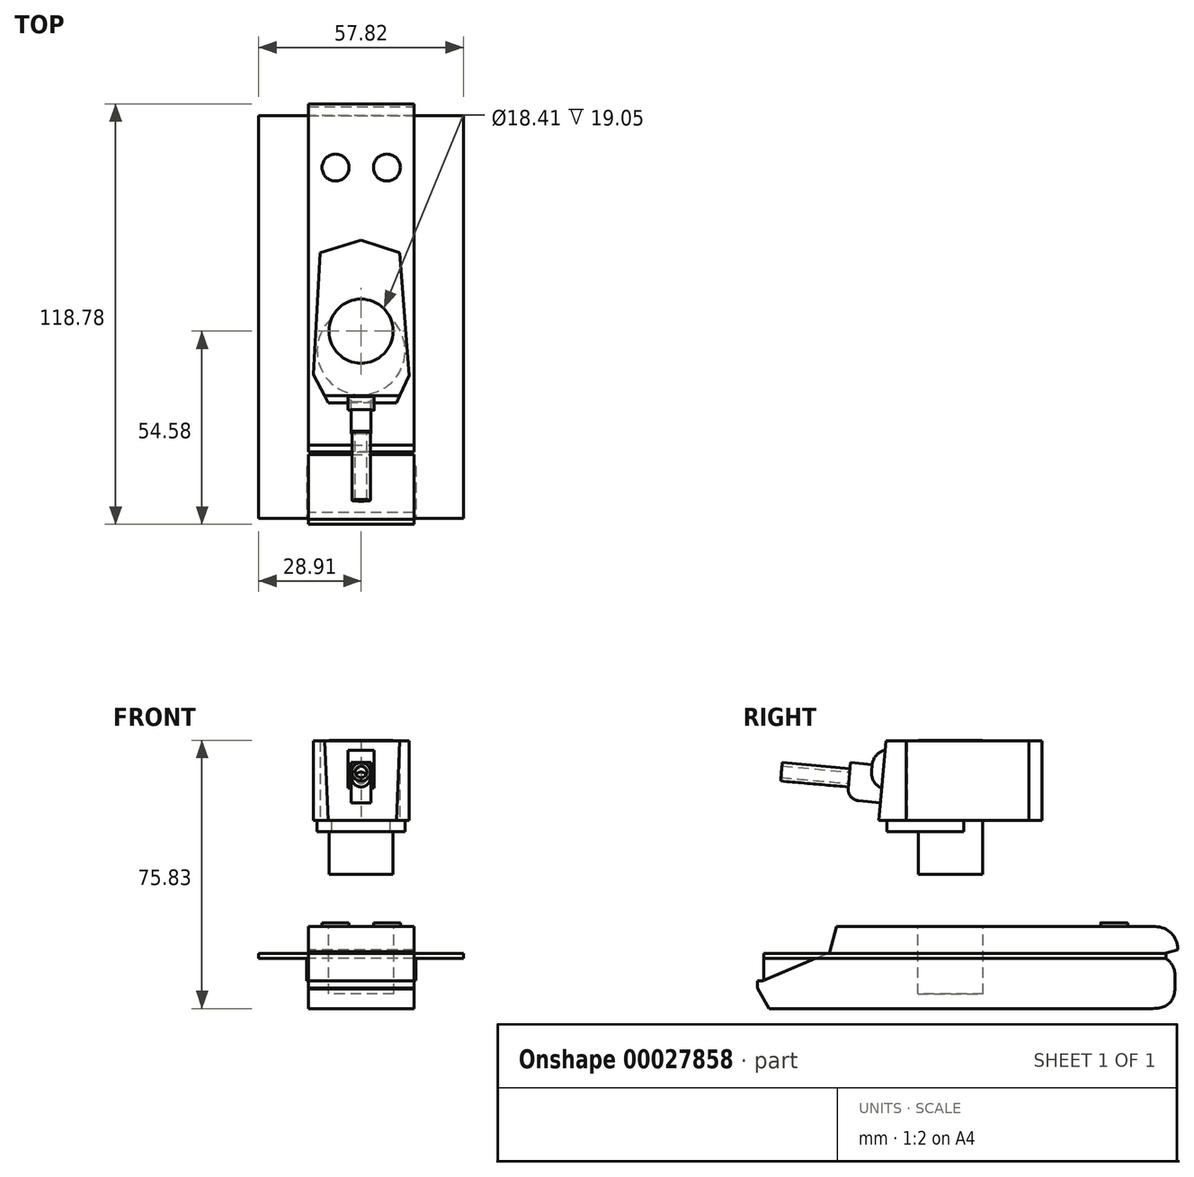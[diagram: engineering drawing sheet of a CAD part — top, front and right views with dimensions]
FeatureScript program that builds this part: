
annotation { "Feature Type Name" : "Feature", "Feature Type Description" : "" }
export const myFeature = defineFeature(function(context is Context, id is Id, definition is map)
    precondition{}
    {
        {
            var Q0;
            Q0=qCreatedBy(makeId("Top.planeOp"),FACE);
            var sketch = newSketch(context, id + "F0", { "sketchPlane" : qUnion([Q0])});
            skPoint(sketch, "E0.rect.middle", {"position": v(0, 0) * mm});
            skCircle(sketch, "E1", {"center": v(0, 0) * mm, "radius": 9.06 * mm});
            skLineSegment(sketch, "E2", {"start": v(0, 25.77) * mm, "end": v(10.93, 22.14) * mm});
            skLineSegment(sketch, "E3", {"start": v(10.93, 22.14) * mm, "end": v(13.54, -12.57) * mm});
            skLineSegment(sketch, "E4", {"start": v(0, 25.77) * mm, "end": v(-11.58, 22.14) * mm});
            skLineSegment(sketch, "E5", {"start": v(-11.58, 22.14) * mm, "end": v(-13.46, -12.28) * mm});
            skLineSegment(sketch, "E6", {"start": v(-13.46, -12.28) * mm, "end": v(-7.68, -23.37) * mm});
            skLineSegment(sketch, "E7", {"start": v(-7.68, -23.37) * mm, "end": v(8.63, -23.37) * mm});
            skLineSegment(sketch, "E8", {"start": v(8.63, -23.37) * mm, "end": v(13.54, -12.57) * mm});
            skCircle(sketch, "E9", {"center": v(0, -5.56) * mm, "radius": 12.41 * mm});
            skSolve(sketch);
        }
        {
            var Q0;
            {var subQ0=sQuery(id+"F0.wireOp",EDGE,"E9");var subQ1=sQuery(id+"F0.wireOp",EDGE,"E1");var subQ3=makeQuery(id+"F0.imprint","INTERSECT",VERTEX,{"disambiguationData":[OD(0.0)],"derivedFrom":[subQ1,subQ0]});Q0=makeQuery(id+"F0.imprint","IMPRINT",FACE,{"disambiguationData":[TD([[makeQuery(id+"F0.imprint","IMPRINT",EDGE,{"disambiguationData":[TD([[subQ3,-1.0]])],"derivedFrom":subQ1}),-1.0]])]});}
            var Q1;
            Q1=makeQuery(id+"F0.imprint","IMPRINT",FACE,{"disambiguationData":[TD([[makeQuery(id+"F0.imprint","IMPRINT",EDGE,{"derivedFrom":sQuery(id+"F0.wireOp",EDGE,"E2")}),-1.0]])]});
            extrude(context, id + "F1", {"entities" : qUnion([Q0, Q1]), "depth" : 22.5 * mm});
        }
        {
            var Q0;
            {var subQ0=sQuery(id+"F0.wireOp",EDGE,"E9");var subQ1=sQuery(id+"F0.wireOp",EDGE,"E1");var subQ3=makeQuery(id+"F0.imprint","INTERSECT",VERTEX,{"disambiguationData":[OD(0.0)],"derivedFrom":[subQ1,subQ0]});Q0=makeQuery(id+"F0.imprint","IMPRINT",FACE,{"disambiguationData":[TD([[makeQuery(id+"F0.imprint","IMPRINT",EDGE,{"disambiguationData":[TD([[subQ3,-1.0]])],"derivedFrom":subQ1}),1.0]])]});}
            var Q1;
            {var subQ0=sQuery(id+"F0.wireOp",EDGE,"E9");var subQ1=sQuery(id+"F0.wireOp",EDGE,"E1");var subQ3=makeQuery(id+"F0.imprint","INTERSECT",VERTEX,{"disambiguationData":[OD(0.0)],"derivedFrom":[subQ1,subQ0]});Q1=makeQuery(id+"F0.imprint","IMPRINT",FACE,{"disambiguationData":[TD([[makeQuery(id+"F0.imprint","IMPRINT",EDGE,{"disambiguationData":[TD([[subQ3,1.0]])],"derivedFrom":subQ1}),1.0]])]});}
            extrude(context, id + "F2", {"entities" : qUnion([Q0, Q1]), "depth" : 22.7 * mm, "hasSecondDirection" : true, "secondDirectionOppositeDirection" : true, "secondDirectionDepth" : 15.2 * mm});
        }
        {
            var Q0;
            Q0=makeQuery(id+"F1.opExtrude","CAP_EDGE",EDGE,{"disambiguationData":[OSD([sQuery(id+"F0.wireOp",EDGE,"E7")])],"isStart":false});
            chamfer(context, id + "F3", {"entities" : qUnion([Q0]), "chamferType" : ChamferType.OFFSET_ANGLE, "width" : 5.08 * mm, "oppositeDirection" : false, "angle" : 85 * degree, "tangentPropagation" : true});
        }
        {
            var Q0;
            Q0=makeQuery(id+"F3.opChamfer","BLEND_FACE",FACE,{"disambiguationData":[OSD([sQuery(id+"F0.wireOp",EDGE,"E7")])]});
            var sketch = newSketch(context, id + "F4", { "sketchPlane" : qUnion([Q0])});
            skLineSegment(sketch, "E10.rect.top", {"start": v(-2.78, 13.83) * mm, "end": v(2.78, 13.83) * mm});
            skPoint(sketch, "E10.rect.middle", {"position": v(0, 9.54) * mm});
            skCircle(sketch, "E11", {"center": v(0, 9.54) * mm, "radius": 2.62 * mm});
            skCircle(sketch, "E12", {"center": v(0, 9.54) * mm, "radius": 1.62 * mm});
            skPoint(sketch, "E10.rect.bottom.end.orphan", {"position": v(2.78, 5.25) * mm});
            skPoint(sketch, "E10.rect.bottom.start.orphan", {"position": v(-2.78, 5.25) * mm});
            skLineSegment(sketch, "E13", {"start": v(-2.78, 13.83) * mm, "end": v(-2.78, 3.3) * mm});
            skLineSegment(sketch, "E14", {"start": v(-2.78, 3.3) * mm, "end": v(2.84, 3.3) * mm});
            skLineSegment(sketch, "E15", {"start": v(2.84, 3.3) * mm, "end": v(2.78, 13.83) * mm});
            skSolve(sketch);
        }
        {
            var Q0;
            Q0=makeQuery(id+"F4.imprint","IMPRINT",FACE,{"disambiguationData":[TD([[makeQuery(id+"F4.imprint","IMPRINT",EDGE,{"derivedFrom":sQuery(id+"F4.wireOp",EDGE,"E11")}),1.0]])]});
            extrude(context, id + "F5", {"entities" : qUnion([Q0]), "operationType" : NewBodyOperationType.ADD, "depth" : 28.63 * mm});
        }
        {
            var Q0;
            Q0=makeQuery(id+"F4.imprint","IMPRINT",FACE,{"disambiguationData":[TD([[makeQuery(id+"F4.imprint","IMPRINT",EDGE,{"derivedFrom":sQuery(id+"F4.wireOp",EDGE,"E11")}),1.0]])]});
            var Q1;
            Q1=makeQuery(id+"F4.imprint","IMPRINT",FACE,{"disambiguationData":[TD([[makeQuery(id+"F4.imprint","IMPRINT",EDGE,{"derivedFrom":sQuery(id+"F4.wireOp",EDGE,"E12")}),1.0]])]});
            var Q2;
            Q2=makeQuery(id+"F4.imprint","IMPRINT",FACE,{"disambiguationData":[TD([[makeQuery(id+"F4.imprint","IMPRINT",EDGE,{"derivedFrom":sQuery(id+"F4.wireOp",EDGE,"E10.rect.top")}),-1.0]])]});
            extrude(context, id + "F6", {"entities" : qUnion([Q0, Q1, Q2]), "operationType" : NewBodyOperationType.ADD, "depth" : 9.42 * mm});
        }
        {
            var Q0;
            Q0=makeQuery(id+"F6.opExtrude","CAP_EDGE",EDGE,{"disambiguationData":[OSD([sQuery(id+"F4.wireOp",EDGE,"E14")])],"isStart":false});
            fillet(context, id + "F7", {"entities" : qUnion([Q0]), "radius" : 3.23 * mm, "tangentPropagation" : true, "allowEdgeOverflow" : false});
        }
        {
            var Q0;
            {var subQ0=sQuery(id+"F0.wireOp",EDGE,"E7");var subQ2=sQuery(id+"F0.wireOp",EDGE,"E6");Q0=makeQuery(id+"F5.boolean.opBoolean","SPLIT",FACE,{"disambiguationData":[TD([makeQuery(id+"F1.opExtrude","SWEPT_FACE",FACE,{"disambiguationData":[OSD([subQ2])]})])],"derivedFrom":makeQuery(id+"F3.opChamfer","BLEND_FACE",FACE,{"disambiguationData":[OSD([subQ0])]})});}
            var sketch = newSketch(context, id + "F8", { "sketchPlane" : qUnion([Q0])});
            skPoint(sketch, "E16.rect.middle", {"position": v(0, 15.58) * mm});
            skPoint(sketch, "E16.rect.left.start.orphan", {"position": v(-3.64, 20.82) * mm});
            skPoint(sketch, "E16.rect.right.start.orphan", {"position": v(3.64, 20.82) * mm});
            skPoint(sketch, "E16.rect.top.end.orphan", {"position": v(3.64, 10.34) * mm});
            skPoint(sketch, "E16.rect.top.start.orphan", {"position": v(-3.64, 10.34) * mm});
            skLineSegment(sketch, "E17.rect.bottom", {"start": v(-3.67, 18.18) * mm, "end": v(3.67, 18.18) * mm});
            skLineSegment(sketch, "E17.rect.top", {"start": v(-3.67, 7.4) * mm, "end": v(3.67, 7.4) * mm});
            skLineSegment(sketch, "E17.rect.left", {"start": v(-3.67, 18.18) * mm, "end": v(-3.67, 7.4) * mm});
            skLineSegment(sketch, "E17.rect.right", {"start": v(3.67, 18.18) * mm, "end": v(3.67, 7.4) * mm});
            skPoint(sketch, "E17.rect.middle", {"position": v(0, 12.79) * mm});
            skSolve(sketch);
        }
        {
            var Q0;
            Q0 = qSketchRegion(id + "F8", true);
            extrude(context, id + "F9", {"entities" : qUnion([Q0]), "operationType" : NewBodyOperationType.ADD, "depth" : 3.3 * mm});
        }
        {
            var Q0;
            Q0=makeQuery(id+"F9.opExtrude","CAP_EDGE",EDGE,{"disambiguationData":[OSD([sQuery(id+"F8.wireOp",EDGE,"E17.rect.bottom")])],"isStart":false});
            var Q1;
            {var subQ0=sQuery(id+"F8.wireOp",EDGE,"E17.rect.top");Q1=makeQuery(id+"F9.boolean.opBoolean","SPLIT",EDGE,{"disambiguationData":[TD([makeQuery(id+"F6.opExtrude","SWEPT_FACE",FACE,{"disambiguationData":[OSD([sQuery(id+"F4.wireOp",EDGE,"E15")])]})])],"derivedFrom":makeQuery(id+"F9.opExtrude","CAP_EDGE",EDGE,{"disambiguationData":[OSD([subQ0])],"isStart":false})});}
            var Q2;
            {var subQ0=sQuery(id+"F8.wireOp",EDGE,"E17.rect.top");Q2=makeQuery(id+"F9.boolean.opBoolean","SPLIT",EDGE,{"disambiguationData":[TD([makeQuery(id+"F6.opExtrude","SWEPT_FACE",FACE,{"disambiguationData":[OSD([sQuery(id+"F4.wireOp",EDGE,"E13")])]})])],"derivedFrom":makeQuery(id+"F9.opExtrude","CAP_EDGE",EDGE,{"disambiguationData":[OSD([subQ0])],"isStart":false})});}
            fillet(context, id + "F10", {"entities" : qUnion([Q0, Q1, Q2]), "radius" : 5.08 * mm, "tangentPropagation" : true, "rho" : 0.5, "crossSection" : FilletCrossSection.CONIC, "allowEdgeOverflow" : false});
        }
        {
            var Q0;
            {var subQ0=sQuery(id+"F0.wireOp",EDGE,"E9");var subQ1=sQuery(id+"F0.wireOp",EDGE,"E1");var subQ3=makeQuery(id+"F0.imprint","INTERSECT",VERTEX,{"disambiguationData":[OD(0.0)],"derivedFrom":[subQ1,subQ0]});Q0=makeQuery(id+"F0.imprint","IMPRINT",FACE,{"disambiguationData":[TD([[makeQuery(id+"F0.imprint","IMPRINT",EDGE,{"disambiguationData":[TD([[subQ3,-1.0]])],"derivedFrom":subQ1}),-1.0]])]});}
            extrude(context, id + "F11", {"entities" : qUnion([Q0]), "operationType" : NewBodyOperationType.ADD, "oppositeDirection" : true, "depth" : 3.18 * mm});
        }
        {
            var Q0;
            Q0=qCreatedBy(makeId("Front.planeOp"),FACE);
            var sketch = newSketch(context, id + "F12", { "sketchPlane" : qUnion([Q0])});
            skLineSegment(sketch, "E18.rect.bottom", {"start": v(-14.94, -37.58) * mm, "end": v(14.94, -37.58) * mm});
            skLineSegment(sketch, "E18.rect.top", {"start": v(-14.94, -53.13) * mm, "end": v(14.94, -53.13) * mm});
            skLineSegment(sketch, "E18.rect.left", {"start": v(-14.94, -38.98) * mm, "end": v(-14.94, -53.13) * mm});
            skLineSegment(sketch, "E18.rect.right", {"start": v(14.94, -38.98) * mm, "end": v(14.94, -53.13) * mm});
            skPoint(sketch, "E18.rect.middle", {"position": v(0, -45.36) * mm});
            skLineSegment(sketch, "E19.bottom", {"start": v(14.94, -37.58) * mm, "end": v(28.9, -37.58) * mm});
            skLineSegment(sketch, "E19.top", {"start": v(14.94, -38.98) * mm, "end": v(28.9, -38.98) * mm});
            skLineSegment(sketch, "E19.right", {"start": v(28.9, -37.58) * mm, "end": v(28.9, -38.98) * mm});
            skLineSegment(sketch, "E20.bottom", {"start": v(-14.94, -37.58) * mm, "end": v(-28.9, -37.58) * mm});
            skLineSegment(sketch, "E20.top", {"start": v(-14.94, -38.98) * mm, "end": v(-28.9, -38.98) * mm});
            skLineSegment(sketch, "E20.right", {"start": v(-28.9, -37.58) * mm, "end": v(-28.9, -38.98) * mm});
            skLineSegment(sketch, "E21.top", {"start": v(-14.94, -29.99) * mm, "end": v(14.94, -29.99) * mm});
            skLineSegment(sketch, "E21.left", {"start": v(-14.94, -37.58) * mm, "end": v(-14.94, -29.99) * mm});
            skLineSegment(sketch, "E21.right", {"start": v(14.94, -37.58) * mm, "end": v(14.94, -29.99) * mm});
            skLineSegment(sketch, "E22.bottom", {"start": v(-14.94, -45.36) * mm, "end": v(14.94, -45.36) * mm});
            skLineSegment(sketch, "E22.top", {"start": v(-14.94, -47.39) * mm, "end": v(14.94, -47.39) * mm});
            skLineSegment(sketch, "E22.left", {"start": v(-14.94, -45.36) * mm, "end": v(-14.94, -47.39) * mm});
            skLineSegment(sketch, "E22.right", {"start": v(14.94, -45.36) * mm, "end": v(14.94, -47.39) * mm});
            skLineSegment(sketch, "E23", {"start": v(-14.94, -37.58) * mm, "end": v(-14.94, -38.98) * mm});
            skLineSegment(sketch, "E24", {"start": v(14.94, -37.58) * mm, "end": v(14.94, -38.98) * mm});
            skSolve(sketch);
        }
        {
            var Q0;
            Q0 = qSketchRegion(id + "F12", true);
            extrude(context, id + "F13", {"entities" : qUnion([Q0]), "depth" : 31.96 * mm});
        }
        {
            var Q0;
            Q0=makeQuery(id+"F12.imprint","IMPRINT",FACE,{"disambiguationData":[TD([[makeQuery(id+"F12.imprint","IMPRINT",EDGE,{"derivedFrom":sQuery(id+"F12.wireOp",EDGE,"E22.bottom")}),-1.0]])]});
            extrude(context, id + "F14", {"entities" : qUnion([Q0]), "operationType" : NewBodyOperationType.ADD, "depth" : 54.58 * mm});
        }
        {
            var Q0;
            Q0=makeQuery(id+"F12.imprint","IMPRINT",FACE,{"disambiguationData":[TD([[makeQuery(id+"F12.imprint","IMPRINT",EDGE,{"derivedFrom":sQuery(id+"F12.wireOp",EDGE,"E18.rect.bottom")}),-1.0]])]});
            extrude(context, id + "F15", {"entities" : qUnion([Q0]), "operationType" : NewBodyOperationType.ADD, "depth" : 54.4 * mm});
        }
        {
            var Q0;
            Q0=makeQuery(id+"F12.imprint","IMPRINT",FACE,{"disambiguationData":[TD([[makeQuery(id+"F12.imprint","IMPRINT",EDGE,{"derivedFrom":sQuery(id+"F12.wireOp",EDGE,"E18.rect.bottom")}),1.0]])]});
            extrude(context, id + "F16", {"entities" : qUnion([Q0]), "operationType" : NewBodyOperationType.ADD, "depth" : 34.1 * mm});
        }
        {
            var Q0;
            Q0=makeQuery(id+"F16.opExtrude","CAP_EDGE",EDGE,{"disambiguationData":[OSD([sQuery(id+"F12.wireOp",EDGE,"E21.top")])],"isStart":false});
            chamfer(context, id + "F17", {"entities" : qUnion([Q0]), "chamferType" : ChamferType.OFFSET_ANGLE, "width" : 1.9 * mm, "oppositeDirection" : false, "angle" : 75 * degree, "tangentPropagation" : true});
        }
        {
            var Q0;
            Q0=makeQuery(id+"F15.opExtrude","CAP_EDGE",EDGE,{"disambiguationData":[OSD([sQuery(id+"F12.wireOp",EDGE,"E18.rect.bottom")])],"isStart":false});
            chamfer(context, id + "F18", {"entities" : qUnion([Q0]), "chamferType" : ChamferType.OFFSET_ANGLE, "width" : 19.56 * mm, "oppositeDirection" : false, "angle" : 23 * degree, "tangentPropagation" : true});
        }
        {
            var Q0;
            {var subQ2=sQuery(id+"F12.wireOp",EDGE,"E18.rect.top");Q0=makeQuery(id+"F12.imprint","IMPRINT",FACE,{"disambiguationData":[TD([[makeQuery(id+"F12.imprint","IMPRINT",EDGE,{"derivedFrom":subQ2}),1.0]])]});}
            extrude(context, id + "F19", {"entities" : qUnion([Q0]), "operationType" : NewBodyOperationType.ADD, "depth" : 54.5 * mm});
        }
        {
            var Q0;
            Q0=makeQuery(id+"F12.imprint","IMPRINT",FACE,{"disambiguationData":[TD([[makeQuery(id+"F12.imprint","IMPRINT",EDGE,{"derivedFrom":sQuery(id+"F12.wireOp",EDGE,"E19.bottom")}),-1.0]])]});
            var Q1;
            Q1=makeQuery(id+"F12.imprint","IMPRINT",FACE,{"disambiguationData":[TD([[makeQuery(id+"F12.imprint","IMPRINT",EDGE,{"derivedFrom":sQuery(id+"F12.wireOp",EDGE,"E20.bottom")}),1.0]])]});
            extrude(context, id + "F20", {"entities" : qUnion([Q0, Q1]), "operationType" : NewBodyOperationType.ADD, "depth" : 52.84 * mm});
        }
        {
            var Q0;
            Q0=makeQuery(id+"F20.opExtrude","SWEPT_FACE",FACE,{"disambiguationData":[OSD([sQuery(id+"F12.wireOp",EDGE,"E24")])]});
            var sketch = newSketch(context, id + "F21", { "sketchPlane" : qUnion([Q0])});
            skLineSegment(sketch, "E25", {"start": v(52.84, -38.98) * mm, "end": v(52.84, -45.14) * mm});
            skLineSegment(sketch, "E26", {"start": v(52.84, -45.14) * mm, "end": v(38.13, -38.98) * mm});
            skLineSegment(sketch, "E27", {"start": v(38.13, -38.98) * mm, "end": v(52.84, -38.98) * mm});
            skSolve(sketch);
        }
        {
            var Q0;
            Q0=makeQuery(id+"F21.imprint","IMPRINT",FACE,{"disambiguationData":[TD([[makeQuery(id+"F21.imprint","IMPRINT",EDGE,{"derivedFrom":sQuery(id+"F21.wireOp",EDGE,"E25")}),-1.0]])]});
            var Q1;
            Q1=makeQuery(id+"F21.imprint","IMPRINT",FACE,{"disambiguationData":[TD([[makeQuery(id+"F21.imprint","IMPRINT",EDGE,{"derivedFrom":sQuery(id+"F21.wireOp",EDGE,"E27")}),-1.0]])]});
            extrude(context, id + "F22", {"entities" : qUnion([Q0, Q1]), "operationType" : NewBodyOperationType.ADD, "oppositeDirection" : true, "depth" : 0.5 * mm});
        }
        {
            var Q0;
            Q0=makeQuery(id+"F21.imprint","IMPRINT",FACE,{"disambiguationData":[TD([[makeQuery(id+"F21.imprint","IMPRINT",EDGE,{"derivedFrom":sQuery(id+"F21.wireOp",EDGE,"E25")}),-1.0]])]});
            extrude(context, id + "F23", {"entities" : qUnion([Q0]), "operationType" : NewBodyOperationType.ADD, "oppositeDirection" : true, "depth" : 0.5 * mm});
        }
        {
            var Q0;
            Q0=makeQuery(id+"F20.opExtrude","SWEPT_FACE",FACE,{"disambiguationData":[OSD([sQuery(id+"F12.wireOp",EDGE,"E23")])]});
            var sketch = newSketch(context, id + "F24", { "sketchPlane" : qUnion([Q0])});
            skLineSegment(sketch, "E28", {"start": v(-52.84, -37.58) * mm, "end": v(-52.84, -45.25) * mm});
            skLineSegment(sketch, "E29", {"start": v(-52.84, -45.25) * mm, "end": v(-34.84, -37.58) * mm});
            skLineSegment(sketch, "E30", {"start": v(-34.84, -37.58) * mm, "end": v(-52.84, -37.58) * mm});
            skSolve(sketch);
        }
        {
            var Q0;
            {var subQ14=sQuery(id+"F24.wireOp",EDGE,"E29");Q0=makeQuery(id+"F24.imprint","IMPRINT",FACE,{"disambiguationData":[TD([[makeQuery(id+"F24.imprint","IMPRINT",EDGE,{"derivedFrom":subQ14}),1.0]])]});}
            extrude(context, id + "F25", {"entities" : qUnion([Q0]), "operationType" : NewBodyOperationType.ADD, "oppositeDirection" : true, "depth" : 0.5 * mm});
        }
        {
            var Q0;
            Q0=makeQuery(id+"F19.opExtrude","CAP_EDGE",EDGE,{"disambiguationData":[OSD([sQuery(id+"F12.wireOp",EDGE,"E18.rect.top")])],"isStart":false});
            chamfer(context, id + "F26", {"entities" : qUnion([Q0]), "chamferType" : ChamferType.OFFSET_ANGLE, "width" : 5.6 * mm, "oppositeDirection" : false, "angle" : 30 * degree, "tangentPropagation" : true});
        }
        {
            var Q0;
            Q0=makeQuery(id+"F12.imprint","IMPRINT",FACE,{"disambiguationData":[TD([[makeQuery(id+"F12.imprint","IMPRINT",EDGE,{"derivedFrom":sQuery(id+"F12.wireOp",EDGE,"E18.rect.bottom")}),1.0]])]});
            extrude(context, id + "F27", {"entities" : qUnion([Q0]), "operationType" : NewBodyOperationType.ADD, "oppositeDirection" : true, "depth" : 64.2 * mm});
        }
        {
            var Q0;
            Q0=makeQuery(id+"F12.imprint","IMPRINT",FACE,{"disambiguationData":[TD([[makeQuery(id+"F12.imprint","IMPRINT",EDGE,{"derivedFrom":sQuery(id+"F12.wireOp",EDGE,"E18.rect.bottom")}),-1.0]])]});
            var Q1;
            Q1=makeQuery(id+"F12.imprint","IMPRINT",FACE,{"disambiguationData":[TD([[makeQuery(id+"F12.imprint","IMPRINT",EDGE,{"derivedFrom":sQuery(id+"F12.wireOp",EDGE,"E22.bottom")}),-1.0]])]});
            var Q2;
            {var subQ2=sQuery(id+"F12.wireOp",EDGE,"E18.rect.top");Q2=makeQuery(id+"F12.imprint","IMPRINT",FACE,{"disambiguationData":[TD([[makeQuery(id+"F12.imprint","IMPRINT",EDGE,{"derivedFrom":subQ2}),1.0]])]});}
            var Q3;
            Q3=makeQuery(id+"F12.imprint","IMPRINT",FACE,{"disambiguationData":[TD([[makeQuery(id+"F12.imprint","IMPRINT",EDGE,{"derivedFrom":sQuery(id+"F12.wireOp",EDGE,"E19.bottom")}),-1.0]])]});
            var Q4;
            Q4=makeQuery(id+"F12.imprint","IMPRINT",FACE,{"disambiguationData":[TD([[makeQuery(id+"F12.imprint","IMPRINT",EDGE,{"derivedFrom":sQuery(id+"F12.wireOp",EDGE,"E20.bottom")}),1.0]])]});
            extrude(context, id + "F28", {"entities" : qUnion([Q0, Q1, Q2, Q3, Q4]), "operationType" : NewBodyOperationType.ADD, "oppositeDirection" : true, "depth" : 60.88 * mm});
        }
        {
            var Q0;
            {var subQ0=sQuery(id+"F12.wireOp",EDGE,"E21.top");Q0=makeQuery(id+"F27.boolean.opBoolean","MERGE",FACE,{"derivedFrom":[makeQuery(id+"F16.boolean.opBoolean","MERGE",FACE,{"derivedFrom":[makeQuery(id+"F13.opExtrude","SWEPT_FACE",FACE,{"disambiguationData":[OSD([subQ0])]}),makeQuery(id+"F16.opExtrude","SWEPT_FACE",FACE,{"disambiguationData":[OSD([subQ0])]})]}),makeQuery(id+"F27.opExtrude","SWEPT_FACE",FACE,{"disambiguationData":[OSD([subQ0])]})]});}
            var sketch = newSketch(context, id + "F29", { "sketchPlane" : qUnion([Q0])});
            skCircle(sketch, "E31", {"center": v(0, 0) * mm, "radius": 9.2 * mm});
            skSolve(sketch);
        }
        {
            var Q0;
            Q0=makeQuery(id+"F29.imprint","IMPRINT",FACE,{"disambiguationData":[TD([[makeQuery(id+"F29.imprint","IMPRINT",EDGE,{"derivedFrom":sQuery(id+"F29.wireOp",EDGE,"E31")}),1.0]])]});
            extrude(context, id + "F30", {"entities" : qUnion([Q0]), "operationType" : NewBodyOperationType.REMOVE, "oppositeDirection" : true, "depth" : 19.05 * mm});
        }
        {
            var Q0;
            Q0=makeQuery(id+"F27.opExtrude","CAP_EDGE",EDGE,{"disambiguationData":[OSD([sQuery(id+"F12.wireOp",EDGE,"E21.top")])],"isStart":false});
            fillet(context, id + "F31", {"entities" : qUnion([Q0]), "radius" : 6.35 * mm, "tangentPropagation" : true, "allowEdgeOverflow" : false});
        }
        {
            var Q0;
            Q0=makeQuery(id+"F27.opExtrude","CAP_EDGE",EDGE,{"disambiguationData":[OSD([sQuery(id+"F12.wireOp",EDGE,"E18.rect.bottom")])],"isStart":false});
            chamfer(context, id + "F32", {"entities" : qUnion([Q0]), "chamferType" : ChamferType.OFFSET_ANGLE, "width" : 3.8 * mm, "oppositeDirection" : false, "angle" : 15 * degree, "tangentPropagation" : true});
        }
        {
            var Q0;
            Q0=makeQuery(id+"F28.opExtrude","CAP_FACE",FACE,{"disambiguationData":[OSD([sQuery(id+"F12.wireOp",EDGE,"E18.rect.top"),sQuery(id+"F12.wireOp",EDGE,"E18.rect.left"),sQuery(id+"F12.wireOp",EDGE,"E18.rect.right"),sQuery(id+"F12.wireOp",EDGE,"E19.bottom"),sQuery(id+"F12.wireOp",EDGE,"E19.top"),sQuery(id+"F12.wireOp",EDGE,"E19.right"),sQuery(id+"F12.wireOp",EDGE,"E20.bottom"),sQuery(id+"F12.wireOp",EDGE,"E20.top"),sQuery(id+"F12.wireOp",EDGE,"E20.right"),sQuery(id+"F12.wireOp",EDGE,"E18.rect.bottom"),sQuery(id+"F12.wireOp",EDGE,"E22.left"),sQuery(id+"F12.wireOp",EDGE,"E22.right")])],"isStart":false});
            var sketch = newSketch(context, id + "F33", { "sketchPlane" : qUnion([Q0])});
            skLineSegment(sketch, "E32", {"start": v(-14.94, -38.98) * mm, "end": v(-14.94, -53.13) * mm});
            skLineSegment(sketch, "E33", {"start": v(-14.94, -53.13) * mm, "end": v(14.94, -53.13) * mm});
            skLineSegment(sketch, "E34", {"start": v(14.94, -53.13) * mm, "end": v(14.94, -38.98) * mm});
            skLineSegment(sketch, "E35", {"start": v(14.94, -38.98) * mm, "end": v(-14.94, -38.98) * mm});
            skSolve(sketch);
        }
        {
            var Q0;
            Q0 = qSketchRegion(id + "F33", true);
            var Q1;
            Q1=makeQuery(id+"F33.imprint","IMPRINT",FACE,{"disambiguationData":[TD([[makeQuery(id+"F33.imprint","IMPRINT",EDGE,{"derivedFrom":sQuery(id+"F33.wireOp",EDGE,"E32")}),1.0]])]});
            extrude(context, id + "F34", {"entities" : qUnion([Q0, Q1]), "operationType" : NewBodyOperationType.ADD, "depth" : 2.58 * mm});
        }
        {
            var Q0;
            Q0=makeQuery(id+"F34.opExtrude","CAP_EDGE",EDGE,{"disambiguationData":[OSD([sQuery(id+"F33.wireOp",EDGE,"E35")])],"isStart":false});
            var Q1;
            Q1=makeQuery(id+"F34.opExtrude","CAP_EDGE",EDGE,{"disambiguationData":[OSD([sQuery(id+"F33.wireOp",EDGE,"E33")])],"isStart":false});
            fillet(context, id + "F35", {"entities" : qUnion([Q0, Q1]), "radius" : 6.37 * mm, "tangentPropagation" : true, "rho" : 0.5, "crossSection" : FilletCrossSection.CONIC, "allowEdgeOverflow" : false});
        }
        {
            var Q0;
            {var subQ0=sQuery(id+"F12.wireOp",EDGE,"E21.top");Q0=makeQuery(id+"F27.boolean.opBoolean","MERGE",FACE,{"derivedFrom":[makeQuery(id+"F16.boolean.opBoolean","MERGE",FACE,{"derivedFrom":[makeQuery(id+"F13.opExtrude","SWEPT_FACE",FACE,{"disambiguationData":[OSD([subQ0])]}),makeQuery(id+"F16.opExtrude","SWEPT_FACE",FACE,{"disambiguationData":[OSD([subQ0])]})]}),makeQuery(id+"F27.opExtrude","SWEPT_FACE",FACE,{"disambiguationData":[OSD([subQ0])]})]});}
            var sketch = newSketch(context, id + "F36", { "sketchPlane" : qUnion([Q0])});
            skCircle(sketch, "E36", {"center": v(-7.22, 46.23) * mm, "radius": 3.81 * mm});
            skCircle(sketch, "E37", {"center": v(7.3, 46.23) * mm, "radius": 3.81 * mm});
            skSolve(sketch);
        }
        {
            var Q0;
            Q0=makeQuery(id+"F36.imprint","IMPRINT",FACE,{"disambiguationData":[TD([[makeQuery(id+"F36.imprint","IMPRINT",EDGE,{"derivedFrom":sQuery(id+"F36.wireOp",EDGE,"E36")}),1.0]])]});
            var Q1;
            Q1=makeQuery(id+"F36.imprint","IMPRINT",FACE,{"disambiguationData":[TD([[makeQuery(id+"F36.imprint","IMPRINT",EDGE,{"derivedFrom":sQuery(id+"F36.wireOp",EDGE,"E37")}),1.0]])]});
            extrude(context, id + "F37", {"entities" : qUnion([Q0, Q1]), "operationType" : NewBodyOperationType.ADD, "depth" : 1.09 * mm});
        }
    });
